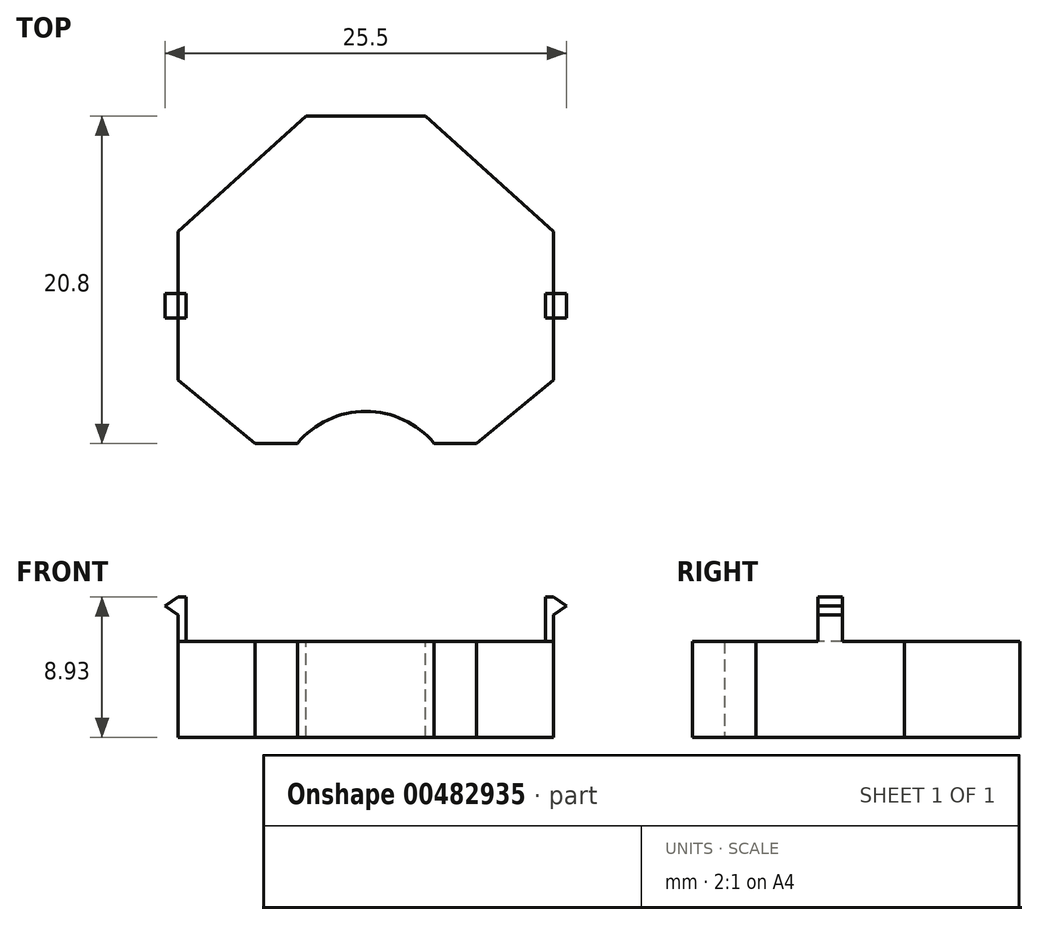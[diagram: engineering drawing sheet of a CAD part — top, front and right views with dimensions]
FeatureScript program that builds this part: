
annotation { "Feature Type Name" : "Feature", "Feature Type Description" : "" }
export const myFeature = defineFeature(function(context is Context, id is Id, definition is map)
    precondition{}
    {
        {
            var Q0;
            Q0=qCreatedBy(makeId("Top.planeOp"),FACE);
            var sketch = newSketch(context, id + "F0", { "sketchPlane" : qUnion([Q0])});
            skLineSegment(sketch, "E0", {"start": v(-39.8, 0) * mm, "end": v(35.24, 0) * mm, "construction": true});
            skLineSegment(sketch, "E1", {"start": v(-11.93, 4.71) * mm, "end": v(-11.93, -4.71) * mm});
            skLineSegment(sketch, "E2", {"start": v(-3.78, -12.05) * mm, "end": v(3.79, -12.05) * mm});
            skLineSegment(sketch, "E3", {"start": v(11.93, -4.71) * mm, "end": v(11.93, 4.71) * mm});
            skLineSegment(sketch, "E4", {"start": v(7.04, 8.75) * mm, "end": v(-7.04, 8.75) * mm});
            skLineSegment(sketch, "E5", {"start": v(-11.93, -4.71) * mm, "end": v(-3.78, -12.05) * mm});
            skLineSegment(sketch, "E6", {"start": v(3.78, -12.05) * mm, "end": v(11.93, -4.71) * mm});
            skLineSegment(sketch, "E7", {"start": v(-11.93, 4.71) * mm, "end": v(-7.04, 8.75) * mm});
            skLineSegment(sketch, "E8", {"start": v(7.04, 8.75) * mm, "end": v(11.93, 4.71) * mm});
            skSolve(sketch);
        }
        {
            var Q0;
            Q0 = qSketchRegion(id + "F0", true);
            extrude(context, id + "F1", {"entities" : qUnion([Q0]), "depth" : 6.1 * mm, "offsetDistance" : 25 * mm});
        }
        {
            var Q0;
            Q0=qCreatedBy(makeId("Front.planeOp"),FACE);
            var sketch = newSketch(context, id + "F2", { "sketchPlane" : qUnion([Q0])});
            skLineSegment(sketch, "E9.bottom", {"start": v(-11.93, 0) * mm, "end": v(-11.43, 0) * mm});
            skLineSegment(sketch, "E9.top", {"start": v(-11.93, -2.83) * mm, "end": v(-11.43, -2.83) * mm});
            skLineSegment(sketch, "E9.left", {"start": v(-11.93, 0) * mm, "end": v(-11.93, -1.69) * mm});
            skLineSegment(sketch, "E9.right", {"start": v(-11.43, 0) * mm, "end": v(-11.43, -2.83) * mm});
            skLineSegment(sketch, "E10.bottom", {"start": v(11.93, 0) * mm, "end": v(11.43, 0) * mm});
            skLineSegment(sketch, "E10.top", {"start": v(11.93, -2.83) * mm, "end": v(11.43, -2.83) * mm});
            skLineSegment(sketch, "E10.left", {"start": v(11.93, 0) * mm, "end": v(11.93, -1.69) * mm});
            skLineSegment(sketch, "E10.right", {"start": v(11.43, 0) * mm, "end": v(11.43, -2.83) * mm});
            skLineSegment(sketch, "E11", {"start": v(-11.93, -2.83) * mm, "end": v(-12.75, -2.26) * mm});
            skLineSegment(sketch, "E12", {"start": v(-12.75, -2.26) * mm, "end": v(-11.93, -1.69) * mm});
            skLineSegment(sketch, "E13", {"start": v(11.93, -2.83) * mm, "end": v(12.75, -2.26) * mm});
            skLineSegment(sketch, "E14", {"start": v(12.75, -2.26) * mm, "end": v(11.93, -1.69) * mm});
            skSolve(sketch);
        }
        {
            var Q0;
            Q0 = qSketchRegion(id + "F2", true);
            extrude(context, id + "F3", {"entities" : qUnion([Q0]), "operationType" : NewBodyOperationType.ADD, "depth" : (1.57 / 2) * mm, "offsetDistance" : 25 * mm, "hasSecondDirection" : true, "secondDirectionOppositeDirection" : true, "secondDirectionDepth" : (1.57 / 2) * mm});
        }
        {
            var Q0;
            Q0=makeQuery(id+"F1.opExtrude","CAP_FACE",FACE,{"disambiguationData":[OSD([sQuery(id+"F0.wireOp",EDGE,"E1"),sQuery(id+"F0.wireOp",EDGE,"E2"),sQuery(id+"F0.wireOp",EDGE,"E3"),sQuery(id+"F0.wireOp",EDGE,"E4"),sQuery(id+"F0.wireOp",EDGE,"E5"),sQuery(id+"F0.wireOp",EDGE,"E6")])],"isStart":false});
            var sketch = newSketch(context, id + "F4", { "sketchPlane" : qUnion([Q0])});
            skCircle(sketch, "E15", {"center": v(0, 12.36) * mm, "radius": 5.65 * mm});
            skPoint(sketch, "E15.centerSnap0", {"position": v(0, 8.75) * mm});
            skSolve(sketch);
        }
        {
            var Q0;
            {var subQ0=sQuery(id+"F4.wireOp",EDGE,"E15");var subQ1=makeQuery(id+"F1.opExtrude","CAP_EDGE",EDGE,{"disambiguationData":[OSD([sQuery(id+"F0.wireOp",EDGE,"E4")])],"isStart":false});var subQ2=makeQuery(id+"F4.imprint","INTERSECT",VERTEX,{"disambiguationData":[OD(0.0)],"derivedFrom":[subQ1,subQ0]});Q0=makeQuery(id+"F4.imprint","IMPRINT",FACE,{"disambiguationData":[TD([[makeQuery(id+"F4.imprint","IMPRINT",EDGE,{"disambiguationData":[TD([[subQ2,1.0]])],"derivedFrom":subQ0}),1.0]])]});}
            extrude(context, id + "F5", {"entities" : qUnion([Q0]), "operationType" : NewBodyOperationType.REMOVE, "endBound" : BoundingType.THROUGH_ALL, "oppositeDirection" : true, "depth" : 25 * mm, "offsetDistance" : 25 * mm});
        }
        {
            var Q0;
            Q0=makeQuery(id+"F1.opExtrude","SWEPT_BODY",BODY,{"disambiguationData":[OSD([sQuery(id+"F0.wireOp",EDGE,"E1"),sQuery(id+"F0.wireOp",EDGE,"E2"),sQuery(id+"F0.wireOp",EDGE,"E3"),sQuery(id+"F0.wireOp",EDGE,"E4"),sQuery(id+"F0.wireOp",EDGE,"E5"),sQuery(id+"F0.wireOp",EDGE,"E6")])]});
            var Q1;
            Q1=sQuery(id+"F0.wireOp",EDGE,"E0");
            transform(context, id + "F6", {"entities" : qUnion([Q0]), "transformType" : TransformType.ROTATION, "transformAxis" : qUnion([Q1]), "angle" : 180 * degree, "makeCopy" : false});
        }
    });
